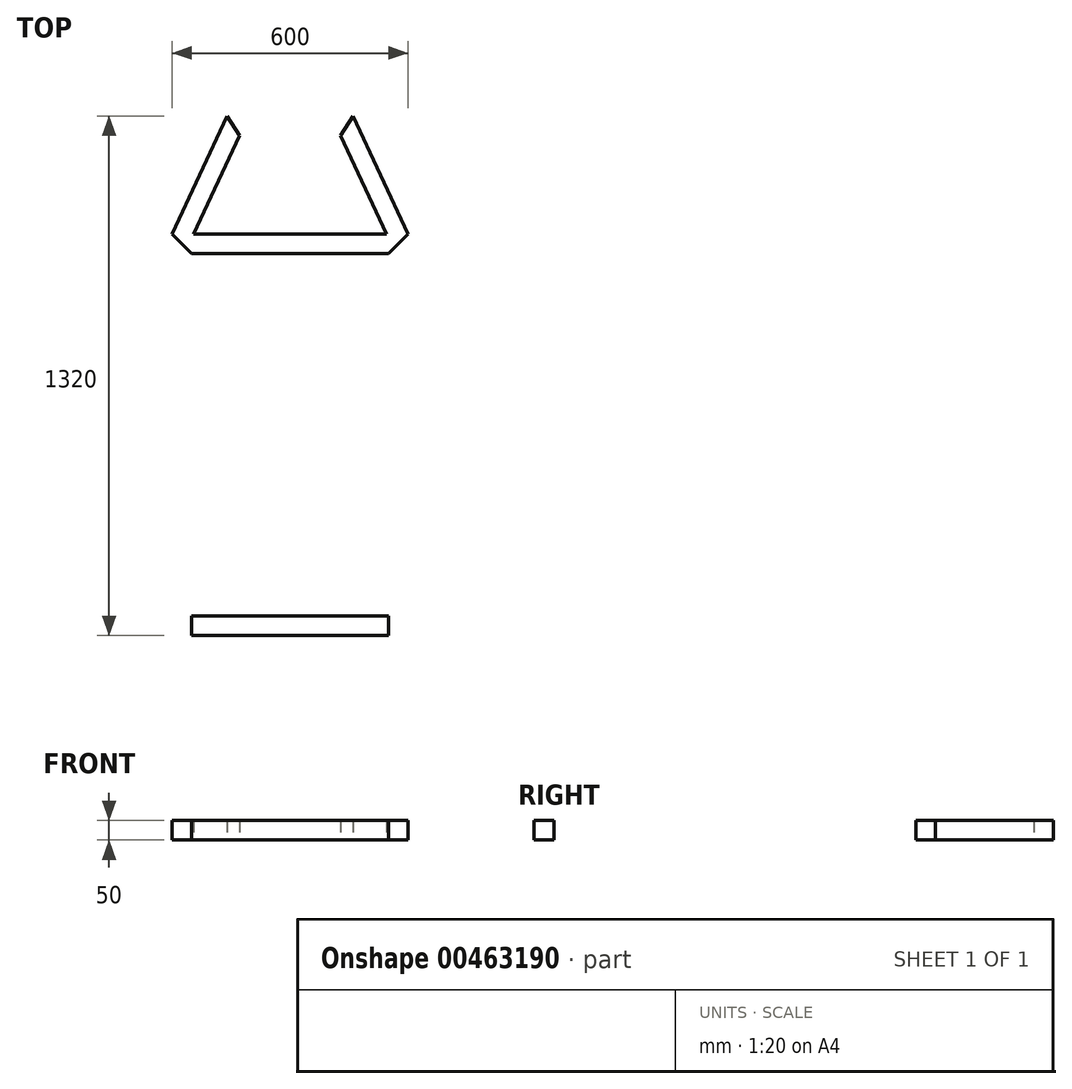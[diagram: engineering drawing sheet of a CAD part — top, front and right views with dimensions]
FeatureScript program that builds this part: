
annotation { "Feature Type Name" : "Feature", "Feature Type Description" : "" }
export const myFeature = defineFeature(function(context is Context, id is Id, definition is map)
    precondition{}
    {
        {
            var Q0;
            Q0=qCreatedBy(makeId("Top.planeOp"),FACE);
            var sketch = newSketch(context, id + "F0", { "sketchPlane" : qUnion([Q0])});
            skLineSegment(sketch, "E0.bottom", {"start": v(0, 0) * mm, "end": v(600, 0) * mm});
            skLineSegment(sketch, "E0.top", {"start": v(0, -1500) * mm, "end": v(600, -1500) * mm});
            skLineSegment(sketch, "E0.left", {"start": v(0, 0) * mm, "end": v(0, -1500) * mm});
            skLineSegment(sketch, "E0.right", {"start": v(600, 0) * mm, "end": v(600, -1500) * mm});
            skLineSegment(sketch, "E1", {"start": v(140, 0) * mm, "end": v(0, -300) * mm});
            skLineSegment(sketch, "E2", {"start": v(0, -300) * mm, "end": v(600, -300) * mm});
            skLineSegment(sketch, "E3", {"start": v(600, -300) * mm, "end": v(460, 0) * mm});
            skLineSegment(sketch, "E4", {"start": v(460, 0) * mm, "end": v(140, 0) * mm});
            skLineSegment(sketch, "E5", {"start": v(171.84, -50) * mm, "end": v(63.93, -281.25) * mm});
            skLineSegment(sketch, "E6", {"start": v(543.2, -296.54) * mm, "end": v(428.16, -50) * mm});
            skLineSegment(sketch, "E7", {"start": v(428.16, -50) * mm, "end": v(171.84, -50) * mm});
            skLineSegment(sketch, "E8", {"start": v(550, -350) * mm, "end": v(550, -1500) * mm});
            skLineSegment(sketch, "E9", {"start": v(50, -1500) * mm, "end": v(50, -350) * mm});
            skLineSegment(sketch, "E10.bottom", {"start": v(50, -1320) * mm, "end": v(550, -1320) * mm});
            skLineSegment(sketch, "E10.top", {"start": v(50, -1270) * mm, "end": v(550, -1270) * mm});
            skLineSegment(sketch, "E10.left", {"start": v(50, -1320) * mm, "end": v(50, -1270) * mm});
            skLineSegment(sketch, "E10.right", {"start": v(550, -1320) * mm, "end": v(550, -1270) * mm});
            skLineSegment(sketch, "E11", {"start": v(0, -300) * mm, "end": v(50, -350) * mm});
            skLineSegment(sketch, "E12", {"start": v(50, -350) * mm, "end": v(550, -350) * mm});
            skLineSegment(sketch, "E13", {"start": v(550, -350) * mm, "end": v(600, -300) * mm});
            skLineSegment(sketch, "E14", {"start": v(171.84, -50) * mm, "end": v(55.18, -300) * mm});
            skLineSegment(sketch, "E15", {"start": v(428.16, -50) * mm, "end": v(544.82, -300) * mm});
            skLineSegment(sketch, "E16", {"start": v(171.84, -50) * mm, "end": v(140, 0) * mm});
            skLineSegment(sketch, "E17", {"start": v(428.16, -50) * mm, "end": v(460, 0) * mm});
            skSolve(sketch);
        }
        {
            var Q0;
            Q0=makeQuery(id+"F0.imprint","IMPRINT",FACE,{"disambiguationData":[TD([[makeQuery(id+"F0.imprint","IMPRINT",EDGE,{"derivedFrom":sQuery(id+"F0.wireOp",EDGE,"E4")}),1.0]])]});
            var Q1;
            {var subQ5=sQuery(id+"F0.wireOp",EDGE,"E1");Q1=makeQuery(id+"F0.imprint","IMPRINT",FACE,{"disambiguationData":[TD([[makeQuery(id+"F0.imprint","IMPRINT",EDGE,{"derivedFrom":subQ5}),1.0]])]});}
            var Q2;
            {var subQ5=sQuery(id+"F0.wireOp",EDGE,"E3");Q2=makeQuery(id+"F0.imprint","IMPRINT",FACE,{"disambiguationData":[TD([[makeQuery(id+"F0.imprint","IMPRINT",EDGE,{"derivedFrom":subQ5}),1.0]])]});}
            var Q3;
            {var subQ0=sQuery(id+"F0.wireOp",EDGE,"E11");Q3=makeQuery(id+"F0.imprint","IMPRINT",FACE,{"disambiguationData":[TD([[makeQuery(id+"F0.imprint","IMPRINT",EDGE,{"derivedFrom":subQ0}),1.0]])]});}
            var Q4;
            {var subQ3=sQuery(id+"F0.wireOp",EDGE,"E10.right");Q4=makeQuery(id+"F0.imprint","IMPRINT",FACE,{"disambiguationData":[TD([[makeQuery(id+"F0.imprint","IMPRINT",EDGE,{"derivedFrom":subQ3}),-1.0]])]});}
            var Q5;
            {var subQ2=sQuery(id+"F0.wireOp",EDGE,"E10.left");Q5=makeQuery(id+"F0.imprint","IMPRINT",FACE,{"disambiguationData":[TD([[makeQuery(id+"F0.imprint","IMPRINT",EDGE,{"derivedFrom":subQ2}),1.0]])]});}
            var Q6;
            Q6=makeQuery(id+"F0.imprint","IMPRINT",FACE,{"disambiguationData":[TD([[makeQuery(id+"F0.imprint","IMPRINT",EDGE,{"derivedFrom":sQuery(id+"F0.wireOp",EDGE,"E10.bottom")}),1.0]])]});
            extrude(context, id + "F1", {"entities" : qUnion([Q0, Q1, Q2, Q3, Q4, Q5, Q6]), "depth" : 50 * mm});
        }
    });
